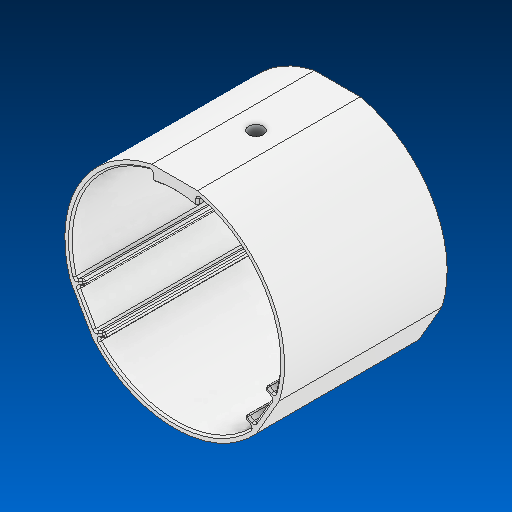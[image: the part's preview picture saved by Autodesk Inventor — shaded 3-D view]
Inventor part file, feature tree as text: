
AUTODESK INVENTOR PART (.ipt)
format: ipt  version: 2022.2 (Build 262287000, 287)  size: 221,696 bytes
history: native  units: in
note: dims shown in document units (in); Inventor stores cm internally (conversion verified against a paired STEP export)
features: chamfer x1
ambient origin geometry x8: Origin, YZ Plane, XZ Plane, XY Plane, X Axis, Y Axis, Z Axis, Center Point
bodies: Solid1 (feature_tree)
feature tree (1):
  chamfer  "Chamfer1"  [1 undecoded]
note: 1 required parameter value undecoded (feature->parameter linkage not recoverable at this tier; creation-order binding heuristic only, values carry confidence <= 0.55)
